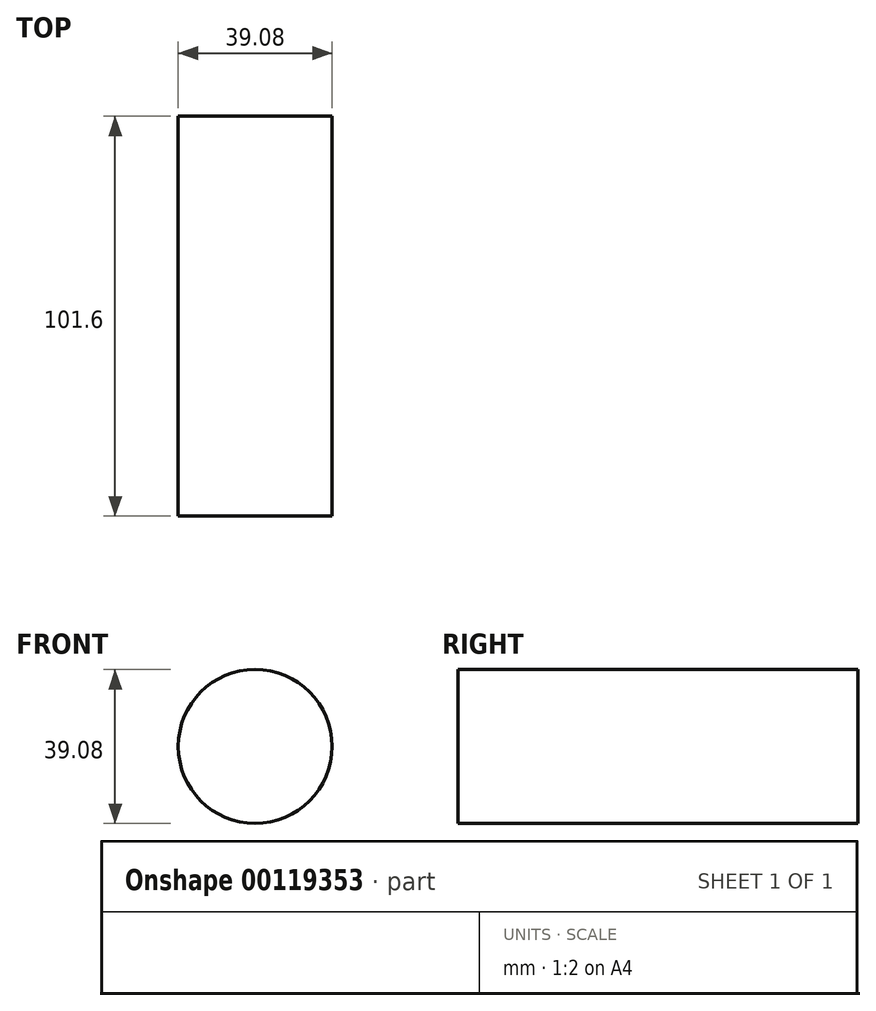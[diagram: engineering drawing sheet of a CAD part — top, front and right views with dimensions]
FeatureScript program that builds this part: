
annotation { "Feature Type Name" : "Feature", "Feature Type Description" : "" }
export const myFeature = defineFeature(function(context is Context, id is Id, definition is map)
    precondition{}
    {
        {
            var Q0;
            Q0=qCreatedBy(makeId("Front.planeOp"),FACE);
            var sketch = newSketch(context, id + "F0", { "sketchPlane" : qUnion([Q0])});
            skCircle(sketch, "E0", {"center": v(0, 0) * mm, "radius": 19.54 * mm});
            skSolve(sketch);
        }
        {
            var Q0;
            Q0=makeQuery(id+"F0.imprint","IMPRINT",FACE,{"disambiguationData":[TD([[makeQuery(id+"F0.imprint","IMPRINT",EDGE,{"derivedFrom":sQuery(id+"F0.wireOp",EDGE,"E0")}),1.0]])]});
            var sketch = newSketch(context, id + "F1", { "sketchPlane" : qUnion([Q0])});
            skSolve(sketch);
        }
        {
            var Q0;
            Q0 = qSketchRegion(id + "F1", true);
            var Q1;
            Q1=makeQuery(id+"F0.imprint","IMPRINT",FACE,{"disambiguationData":[TD([[makeQuery(id+"F0.imprint","IMPRINT",EDGE,{"derivedFrom":sQuery(id+"F0.wireOp",EDGE,"E0")}),1.0]])]});
            extrude(context, id + "F2", {"entities" : qUnion([Q0, Q1]), "depth" : 101.6 * mm});
        }
    });
